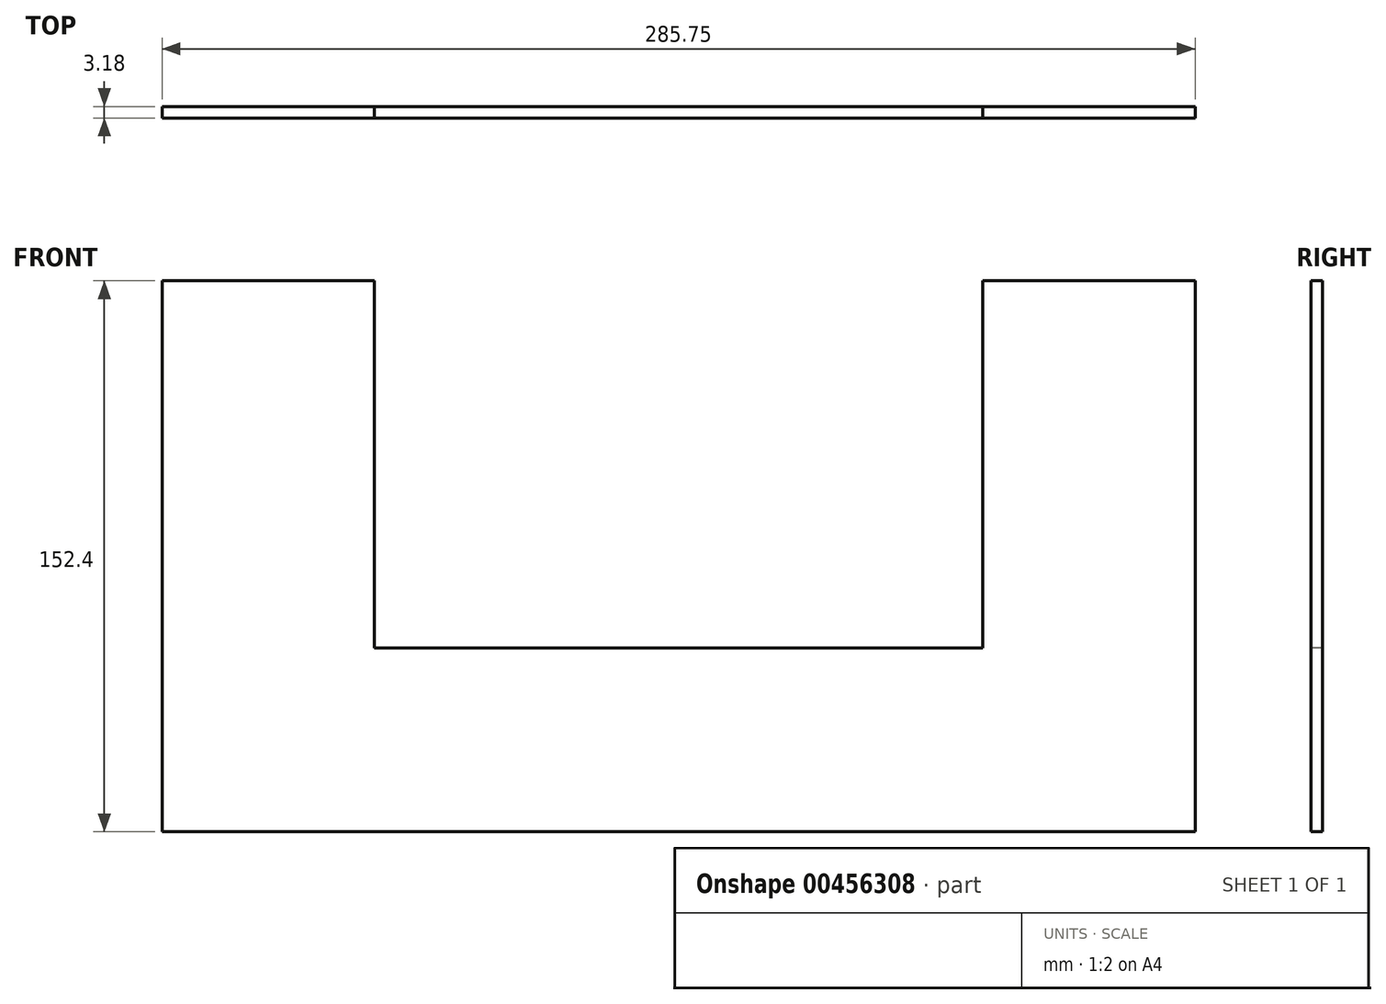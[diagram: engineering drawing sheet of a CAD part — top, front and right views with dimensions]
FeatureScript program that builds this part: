
annotation { "Feature Type Name" : "Feature", "Feature Type Description" : "" }
export const myFeature = defineFeature(function(context is Context, id is Id, definition is map)
    precondition{}
    {
        {
            var Q0;
            Q0=qCreatedBy(makeId("Top.planeOp"),FACE);
            var sketch = newSketch(context, id + "F0", { "sketchPlane" : qUnion([Q0])});
            skLineSegment(sketch, "E0.bottom", {"start": v(0, 0) * mm, "end": v(285.75, 0) * mm});
            skLineSegment(sketch, "E0.top", {"start": v(0, 3.18) * mm, "end": v(285.75, 3.18) * mm});
            skLineSegment(sketch, "E0.left", {"start": v(0, 0) * mm, "end": v(0, 3.18) * mm});
            skLineSegment(sketch, "E0.right", {"start": v(285.75, 0) * mm, "end": v(285.75, 3.18) * mm});
            skSolve(sketch);
        }
        {
            var Q0;
            Q0=makeQuery(id+"F0.imprint","IMPRINT",FACE,{"disambiguationData":[TD([[makeQuery(id+"F0.imprint","IMPRINT",EDGE,{"derivedFrom":sQuery(id+"F0.wireOp",EDGE,"E0.bottom")}),1.0]])]});
            extrude(context, id + "F1", {"entities" : qUnion([Q0]), "depth" : 152.4 * mm});
        }
        {
            var Q0;
            Q0=makeQuery(id+"F1.opExtrude","SWEPT_FACE",FACE,{"disambiguationData":[OSD([sQuery(id+"F0.wireOp",EDGE,"E0.bottom")])]});
            var sketch = newSketch(context, id + "F2", { "sketchPlane" : qUnion([Q0])});
            skLineSegment(sketch, "E1", {"start": v(142.87, 0) * mm, "end": v(142.87, 50.8) * mm});
            skLineSegment(sketch, "E2", {"start": v(0, 76.2) * mm, "end": v(58.74, 76.2) * mm});
            skLineSegment(sketch, "E3", {"start": v(285.75, 76.2) * mm, "end": v(227.01, 76.2) * mm});
            skLineSegment(sketch, "E4", {"start": v(142.87, 50.8) * mm, "end": v(58.74, 50.8) * mm});
            skLineSegment(sketch, "E5", {"start": v(58.74, 50.8) * mm, "end": v(58.74, 152.4) * mm});
            skLineSegment(sketch, "E6", {"start": v(142.87, 50.8) * mm, "end": v(227.01, 50.8) * mm});
            skLineSegment(sketch, "E7", {"start": v(227.01, 50.8) * mm, "end": v(227.01, 152.4) * mm});
            skLineSegment(sketch, "E8", {"start": v(227.01, 152.4) * mm, "end": v(58.74, 152.4) * mm});
            skSolve(sketch);
        }
        {
            var Q0;
            {var subQ5=sQuery(id+"F2.wireOp",EDGE,"E4");Q0=makeQuery(id+"F2.imprint","IMPRINT",FACE,{"disambiguationData":[TD([[makeQuery(id+"F2.imprint","IMPRINT",EDGE,{"derivedFrom":subQ5}),-1.0]])]});}
            extrude(context, id + "F3", {"entities" : qUnion([Q0]), "operationType" : NewBodyOperationType.REMOVE, "oppositeDirection" : true, "depth" : 25.4 * mm});
        }
    });
